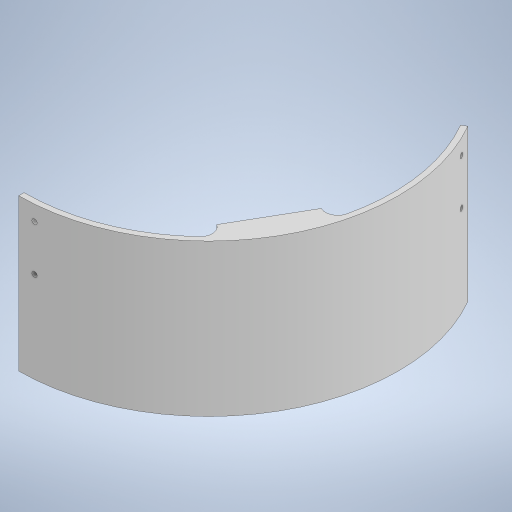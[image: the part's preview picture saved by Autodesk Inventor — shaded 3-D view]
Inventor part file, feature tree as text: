
AUTODESK INVENTOR PART (.ipt)
format: ipt  version: 2023 (Build 270158000, 158)  size: 359,424 bytes
history: native  units: mm
features: sketch x18, extrude x11, hole x7, other x1, fillet x1
ambient origin geometry x8: Origin, YZ Plane, XZ Plane, XY Plane, X Axis, Y Axis, Z Axis, Center Point
bodies: Body1 (feature_tree)
feature tree (38):
  other  "ソリッド1"
  extrude  "押し出し1"  Depth=250.0mm
  extrude  "押し出し2"  Depth=375.0mm TaperAngle=0.0deg
  hole  "穴1"  [1 undecoded]
  hole  "穴2"  [1 undecoded]
  extrude  "押し出し3"  Depth=30.0mm TaperAngle=360.0deg
  extrude  "押し出し4"  Depth=10.0mm
  hole  "穴4"  [1 undecoded]
  hole  "穴5"  [1 undecoded]
  extrude  "押し出し6"  Depth=330.0mm TaperAngle=0.0deg
  extrude  "押し出し7"  Depth=118.0mm
  extrude  "押し出し8"  Depth=30.0mm TaperAngle=360.0deg
  extrude  "押し出し9"  Depth=330.0mm TaperAngle=0.0deg
  extrude  "押し出し11"  Depth=30.0mm
  extrude  "押し出し13"  Depth=30.0mm
  extrude  "押し出し15"  Depth=243.0mm
  fillet  "フィレット1"  Radius=330.0mm
  hole  "穴6"  [1 undecoded]
  hole  "穴7"  [1 undecoded]
  hole  "穴8"  [1 undecoded]
  sketch  "スケッチ1"
  sketch  "スケッチ2"
  sketch  "スケッチ3"
  sketch  "スケッチ4"
  sketch  "スケッチ5"
  sketch  "スケッチ6"
  sketch  "スケッチ8"
  sketch  "スケッチ11"
  sketch  "スケッチ12"
  sketch  "スケッチ13"
  sketch  "スケッチ14"
  sketch  "スケッチ15"
  sketch  "スケッチ17"
  sketch  "スケッチ19"
  sketch  "スケッチ21"
  sketch  "スケッチ22"
  sketch  "スケッチ23"
  sketch  "スケッチ24"
note: 7 required parameter values undecoded (feature->parameter linkage not recoverable at this tier; creation-order binding heuristic only, values carry confidence <= 0.55)
